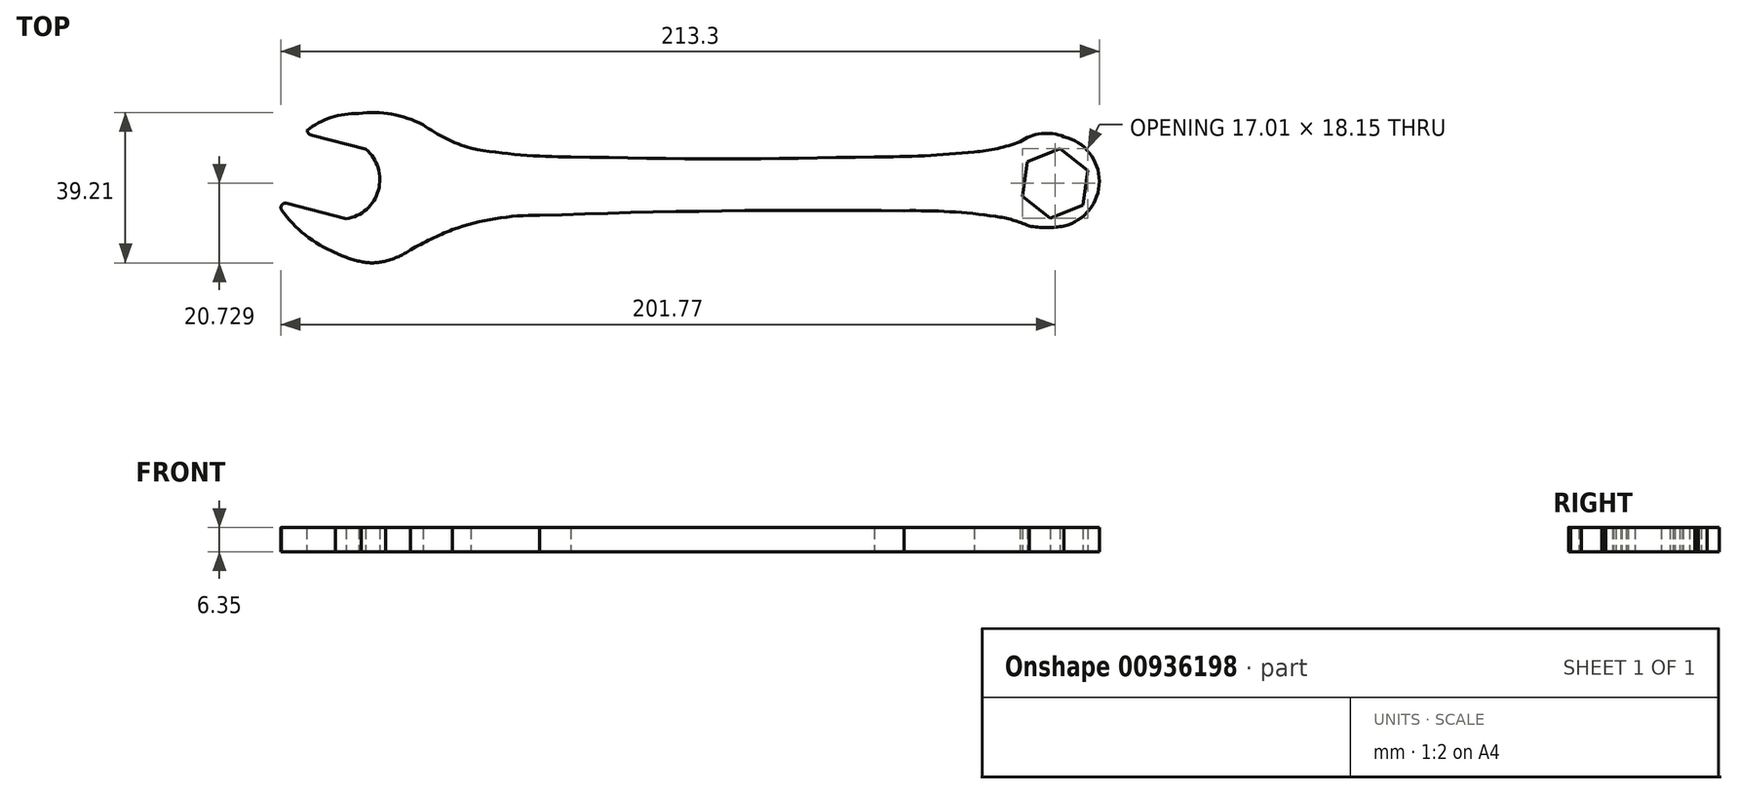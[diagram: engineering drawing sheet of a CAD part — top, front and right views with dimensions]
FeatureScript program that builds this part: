
annotation { "Feature Type Name" : "Feature", "Feature Type Description" : "" }
export const myFeature = defineFeature(function(context is Context, id is Id, definition is map)
    precondition{}
    {
        {
            var Q0;
            Q0=qCreatedBy(makeId("Top.planeOp"),FACE);
            var sketch = newSketch(context, id + "F0", { "sketchPlane" : qUnion([Q0])});
            skLineSegment(sketch, "E0", {"start": v(33.88, 82.18) * mm, "end": v(19.96, 85.77) * mm});
            skLineSegment(sketch, "E1", {"start": v(28.77, 64.04) * mm, "end": v(13.2, 68.06) * mm});
            skArc(sketch, "E2", {"start": v(18.5, 87.07) * mm, "mid": v(19.08, 86.24) * mm, "end": v(19.96, 85.77) * mm});
            skArc(sketch, "E3", {"start": v(32, 91.53) * mm, "mid": v(24.88, 90.46) * mm, "end": v(18.5, 87.07) * mm});
            skArc(sketch, "E4", {"start": v(48.8, 88.6) * mm, "mid": v(40.62, 91.33) * mm, "end": v(32, 91.53) * mm});
            skArc(sketch, "E5", {"start": v(48.8, 88.6) * mm, "mid": v(54.77, 84.97) * mm, "end": v(61.26, 82.41) * mm});
            skArc(sketch, "E6", {"start": v(61.26, 82.41) * mm, "mid": v(74.23, 80.71) * mm, "end": v(87.3, 80.24) * mm});
            skArc(sketch, "E7", {"start": v(87.3, 80.24) * mm, "mid": v(126.88, 79.7) * mm, "end": v(166.46, 80.24) * mm});
            skArc(sketch, "E8", {"start": v(166.46, 80.24) * mm, "mid": v(179.49, 80.5) * mm, "end": v(192.48, 81.48) * mm});
            skArc(sketch, "E9", {"start": v(192.48, 81.48) * mm, "mid": v(198.53, 82.4) * mm, "end": v(204.4, 84.12) * mm});
            skArc(sketch, "E10", {"start": v(215.86, 85.46) * mm, "mid": v(209.95, 86.27) * mm, "end": v(204.4, 84.12) * mm});
            skArc(sketch, "E11", {"start": v(215.86, 62.18) * mm, "mid": v(225.06, 73.82) * mm, "end": v(215.86, 85.46) * mm});
            skArc(sketch, "E12", {"start": v(206.75, 62.18) * mm, "mid": v(211.3, 61.74) * mm, "end": v(215.86, 62.18) * mm});
            skArc(sketch, "E13", {"start": v(206.75, 62.18) * mm, "mid": v(202.49, 63.73) * mm, "end": v(198.05, 64.68) * mm});
            skArc(sketch, "E14", {"start": v(198.05, 64.68) * mm, "mid": v(186.15, 65.88) * mm, "end": v(174.19, 66.13) * mm});
            skArc(sketch, "E15", {"start": v(174.19, 66.13) * mm, "mid": v(126.66, 66.1) * mm, "end": v(79.15, 64.91) * mm});
            skArc(sketch, "E16", {"start": v(79.15, 64.91) * mm, "mid": v(67.64, 64.08) * mm, "end": v(56.46, 61.2) * mm});
            skArc(sketch, "E17", {"start": v(56.46, 61.2) * mm, "mid": v(50.9, 58.76) * mm, "end": v(45.54, 55.92) * mm});
            skArc(sketch, "E18", {"start": v(39.06, 53.04) * mm, "mid": v(42.43, 54.2) * mm, "end": v(45.54, 55.92) * mm});
            skArc(sketch, "E19", {"start": v(32.68, 52.87) * mm, "mid": v(35.88, 52.56) * mm, "end": v(39.06, 53.04) * mm});
            skArc(sketch, "E20", {"start": v(11.9, 66.4) * mm, "mid": v(18.13, 59.82) * mm, "end": v(25.94, 55.22) * mm});
            skArc(sketch, "E21", {"start": v(13.2, 68.06) * mm, "mid": v(12, 67.66) * mm, "end": v(11.9, 66.4) * mm});
            skArc(sketch, "E22", {"start": v(25.94, 55.22) * mm, "mid": v(29.23, 53.82) * mm, "end": v(32.68, 52.87) * mm});
            skArc(sketch, "E23", {"start": v(28.77, 64.04) * mm, "mid": v(37.16, 71.46) * mm, "end": v(33.88, 82.18) * mm});
            skCircle(sketch, "E24.cCircle", {"center": v(213.53, 73.28) * mm, "radius": 7.94 * mm, "construction": true});
            skLineSegment(sketch, "E24.0", {"start": v(222.04, 76.7) * mm, "end": v(220.74, 67.62) * mm});
            skLineSegment(sketch, "E24.1", {"start": v(220.74, 67.62) * mm, "end": v(212.23, 64.2) * mm});
            skLineSegment(sketch, "E24.2", {"start": v(212.23, 64.2) * mm, "end": v(205.02, 69.86) * mm});
            skLineSegment(sketch, "E24.3", {"start": v(205.02, 69.86) * mm, "end": v(206.32, 78.94) * mm});
            skLineSegment(sketch, "E24.4", {"start": v(206.32, 78.94) * mm, "end": v(214.83, 82.35) * mm});
            skLineSegment(sketch, "E24.5", {"start": v(214.83, 82.35) * mm, "end": v(222.04, 76.7) * mm});
            skPoint(sketch, "E24.0.midPoint", {"position": v(221.39, 72.16) * mm});
            skSolve(sketch);
        }
        {
            var Q0;
            Q0=makeQuery(id+"F0.imprint","IMPRINT",FACE,{"disambiguationData":[TD([[makeQuery(id+"F0.imprint","IMPRINT",EDGE,{"derivedFrom":sQuery(id+"F0.wireOp",EDGE,"E0")}),-1.0]])]});
            extrude(context, id + "F1", {"entities" : qUnion([Q0]), "depth" : 6.35 * mm, "offsetDistance" : 25.4 * mm});
        }
    });
